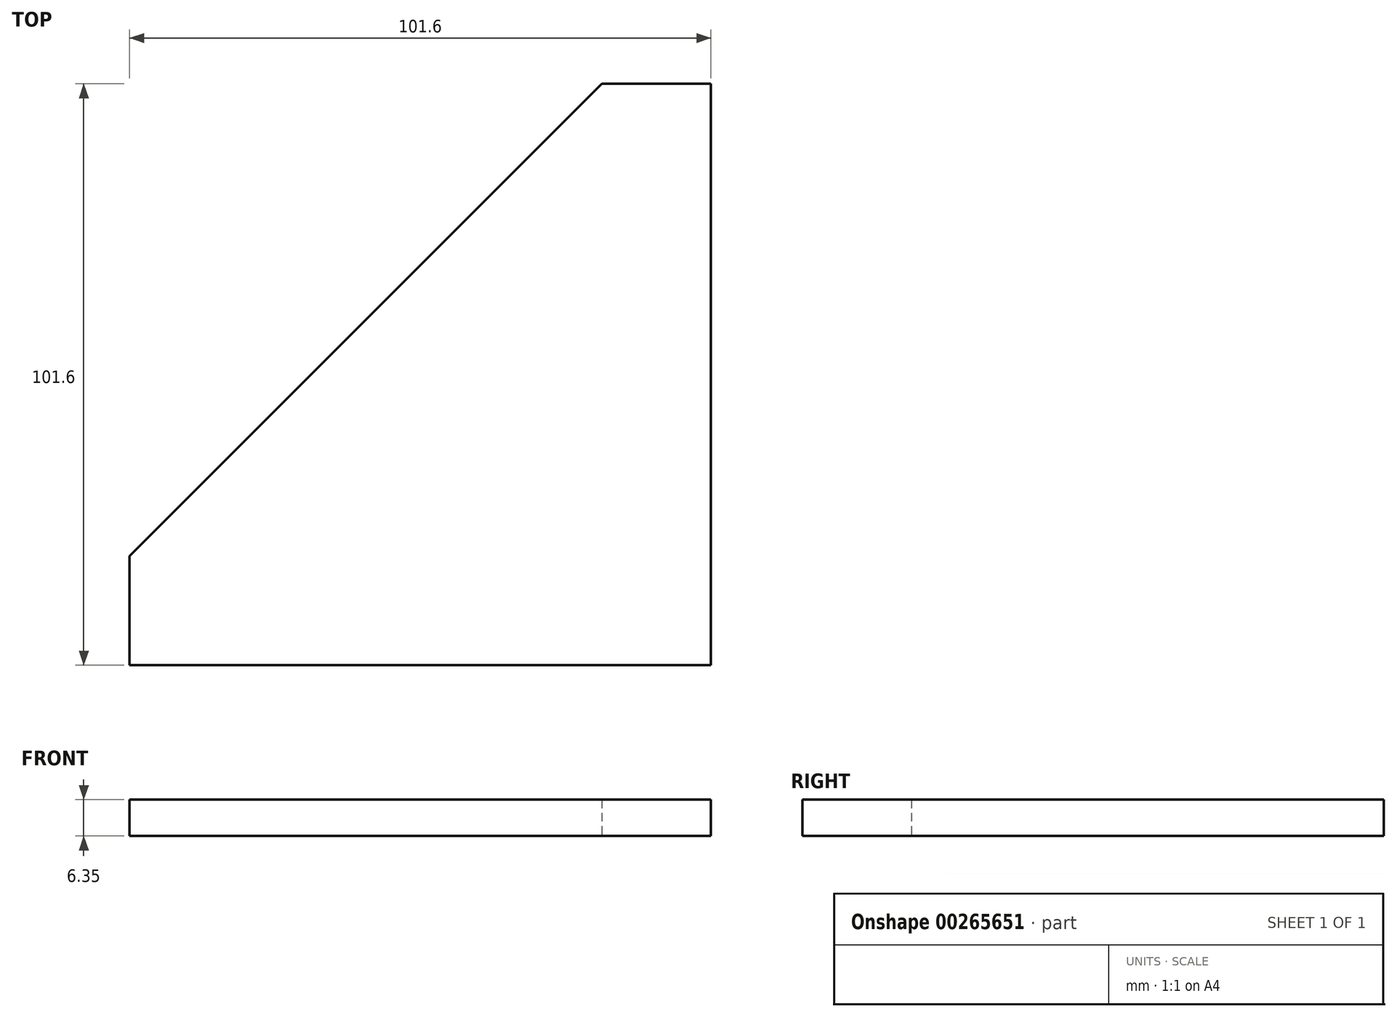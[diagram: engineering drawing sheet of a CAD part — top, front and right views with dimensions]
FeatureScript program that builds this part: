
annotation { "Feature Type Name" : "Feature", "Feature Type Description" : "" }
export const myFeature = defineFeature(function(context is Context, id is Id, definition is map)
    precondition{}
    {
        {
            var Q0;
            Q0=qCreatedBy(makeId("Top.planeOp"),FACE);
            var sketch = newSketch(context, id + "F0", { "sketchPlane" : qUnion([Q0])});
            skLineSegment(sketch, "E0", {"start": v(0, 101.6) * mm, "end": v(0, 0) * mm});
            skLineSegment(sketch, "E1", {"start": v(0, 0) * mm, "end": v(-101.6, 0) * mm});
            skLineSegment(sketch, "E2", {"start": v(-101.6, 0) * mm, "end": v(-101.6, 19.05) * mm});
            skLineSegment(sketch, "E3", {"start": v(-101.6, 19.05) * mm, "end": v(-19.05, 101.6) * mm});
            skLineSegment(sketch, "E4", {"start": v(-19.05, 101.6) * mm, "end": v(0, 101.6) * mm});
            skSolve(sketch);
        }
        {
            var Q0;
            Q0=makeQuery(id+"F0.imprint","IMPRINT",FACE,{"disambiguationData":[TD([[makeQuery(id+"F0.imprint","IMPRINT",EDGE,{"derivedFrom":sQuery(id+"F0.wireOp",EDGE,"E0")}),-1.0]])]});
            extrude(context, id + "F1", {"entities" : qUnion([Q0]), "depth" : 6.35 * mm});
        }
    });
